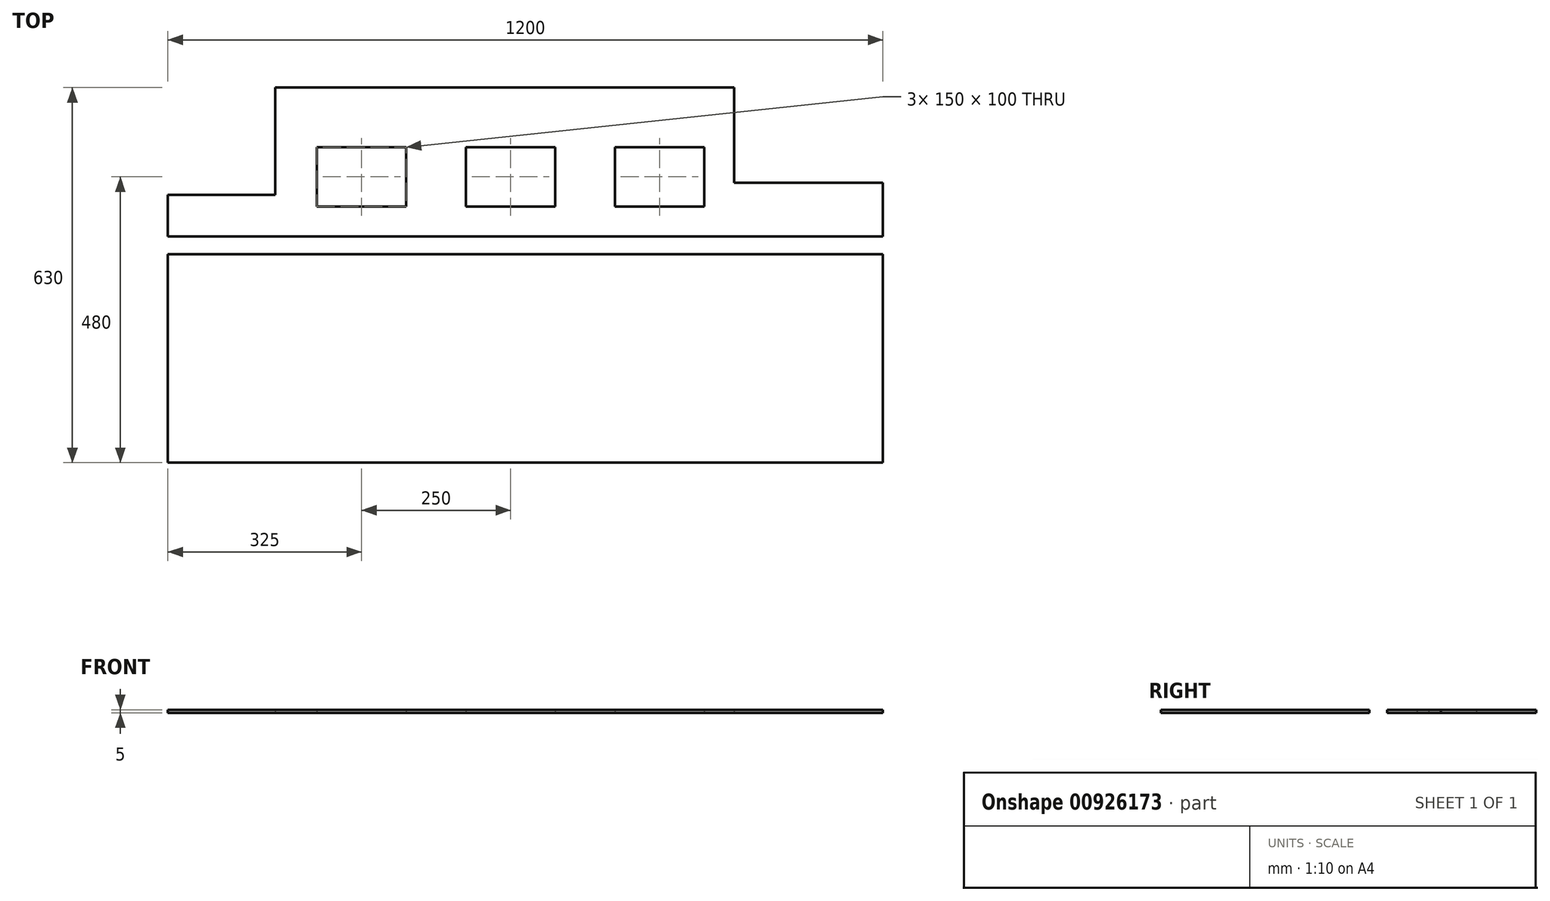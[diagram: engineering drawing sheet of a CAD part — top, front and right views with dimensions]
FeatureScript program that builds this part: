
annotation { "Feature Type Name" : "Feature", "Feature Type Description" : "" }
export const myFeature = defineFeature(function(context is Context, id is Id, definition is map)
    precondition{}
    {
        {
            var Q0;
            Q0=qCreatedBy(makeId("Top.planeOp"),FACE);
            var sketch = newSketch(context, id + "F0", { "sketchPlane" : qUnion([Q0])});
            skLineSegment(sketch, "E0.bottom", {"start": v(-600, -350) * mm, "end": v(600, -350) * mm});
            skLineSegment(sketch, "E0.top", {"start": v(-600, 0) * mm, "end": v(600, 0) * mm});
            skLineSegment(sketch, "E0.left", {"start": v(-600, -350) * mm, "end": v(-600, 0) * mm});
            skLineSegment(sketch, "E0.right", {"start": v(600, -350) * mm, "end": v(600, 0) * mm});
            skLineSegment(sketch, "E1.bottom", {"start": v(-600, 30) * mm, "end": v(600, 30) * mm});
            skLineSegment(sketch, "E1.top", {"start": v(-600, 280) * mm, "end": v(600, 280) * mm});
            skLineSegment(sketch, "E1.left", {"start": v(-600, 30) * mm, "end": v(-600, 280) * mm});
            skLineSegment(sketch, "E1.right", {"start": v(600, 30) * mm, "end": v(600, 280) * mm});
            skLineSegment(sketch, "E2.bottom", {"start": v(-600, 280) * mm, "end": v(-420, 280) * mm});
            skLineSegment(sketch, "E2.top", {"start": v(-600, 100) * mm, "end": v(-420, 100) * mm});
            skLineSegment(sketch, "E2.left", {"start": v(-600, 280) * mm, "end": v(-600, 100) * mm});
            skLineSegment(sketch, "E2.right", {"start": v(-420, 280) * mm, "end": v(-420, 100) * mm});
            skLineSegment(sketch, "E3.bottom", {"start": v(-200, 80) * mm, "end": v(-350, 80) * mm});
            skLineSegment(sketch, "E3.top", {"start": v(-200, 180) * mm, "end": v(-350, 180) * mm});
            skLineSegment(sketch, "E3.left", {"start": v(-200, 80) * mm, "end": v(-200, 180) * mm});
            skLineSegment(sketch, "E3.right", {"start": v(-350, 80) * mm, "end": v(-350, 180) * mm});
            skPoint(sketch, "E3.middle", {"position": v(-275, 130) * mm});
            skLineSegment(sketch, "E4.1.0.0", {"start": v(50, 180) * mm, "end": v(-100, 180) * mm});
            skLineSegment(sketch, "E4.1.0.1", {"start": v(50, 80) * mm, "end": v(50, 180) * mm});
            skLineSegment(sketch, "E4.1.0.2", {"start": v(50, 80) * mm, "end": v(-100, 80) * mm});
            skLineSegment(sketch, "E4.1.0.3", {"start": v(-100, 80) * mm, "end": v(-100, 180) * mm});
            skLineSegment(sketch, "E4.2.0.0", {"start": v(300, 180) * mm, "end": v(150, 180) * mm});
            skLineSegment(sketch, "E4.2.0.1", {"start": v(300, 80) * mm, "end": v(300, 180) * mm});
            skLineSegment(sketch, "E4.2.0.2", {"start": v(300, 80) * mm, "end": v(150, 80) * mm});
            skLineSegment(sketch, "E4.2.0.3", {"start": v(150, 80) * mm, "end": v(150, 180) * mm});
            skLineSegment(sketch, "E4.direction1", {"start": v(-350, 180) * mm, "end": v(-100, 180) * mm, "construction": true});
            skLineSegment(sketch, "E5.bottom", {"start": v(600, 280) * mm, "end": v(350, 280) * mm});
            skLineSegment(sketch, "E5.top", {"start": v(600, 120) * mm, "end": v(350, 120) * mm});
            skLineSegment(sketch, "E5.left", {"start": v(600, 280) * mm, "end": v(600, 120) * mm});
            skLineSegment(sketch, "E5.right", {"start": v(350, 280) * mm, "end": v(350, 120) * mm});
            skSolve(sketch);
        }
        {
            var Q0;
            Q0=makeQuery(id+"F0.imprint","IMPRINT",FACE,{"disambiguationData":[TD([[makeQuery(id+"F0.imprint","IMPRINT",EDGE,{"derivedFrom":sQuery(id+"F0.wireOp",EDGE,"E0.bottom")}),1.0]])]});
            var Q1;
            Q1=makeQuery(id+"F0.imprint","IMPRINT",FACE,{"disambiguationData":[TD([[makeQuery(id+"F0.imprint","IMPRINT",EDGE,{"derivedFrom":sQuery(id+"F0.wireOp",EDGE,"E1.bottom")}),1.0]])]});
            extrude(context, id + "F1", {"entities" : qUnion([Q0, Q1]), "depth" : 5 * mm, "offsetDistance" : 25 * mm});
        }
    });
